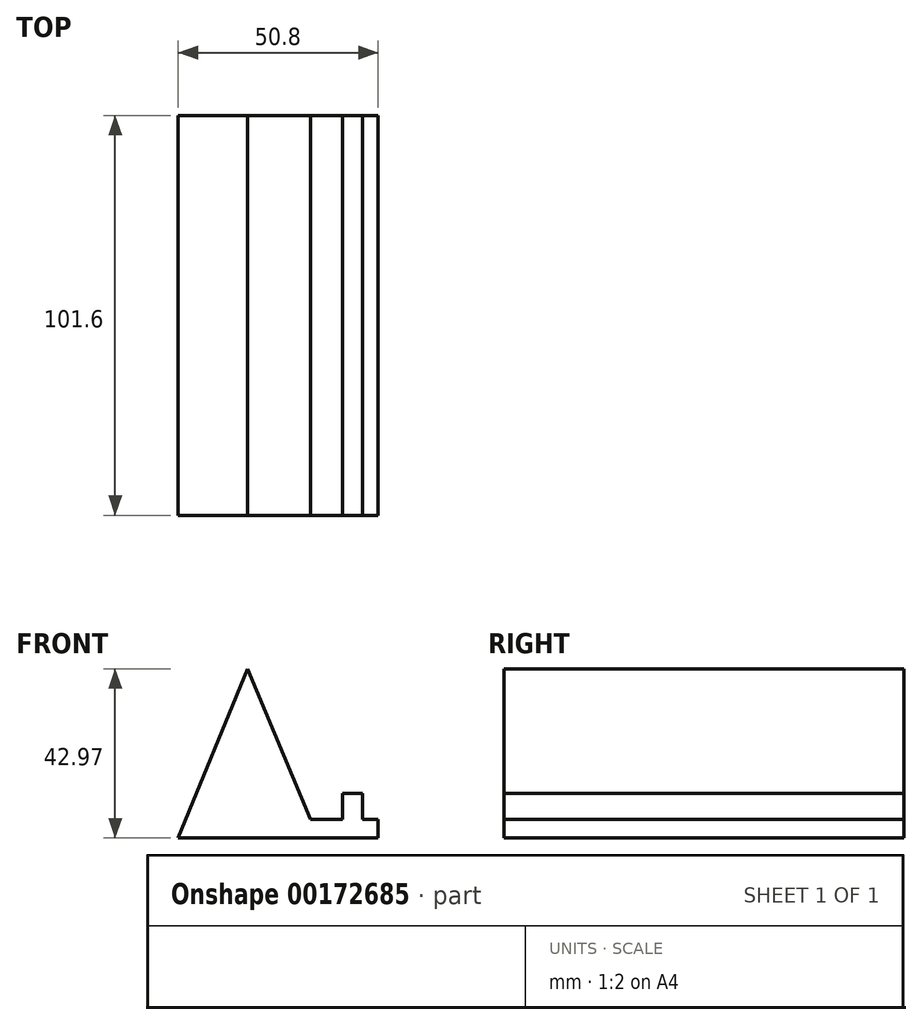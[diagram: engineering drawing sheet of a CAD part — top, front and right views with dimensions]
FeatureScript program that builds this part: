
annotation { "Feature Type Name" : "Feature", "Feature Type Description" : "" }
export const myFeature = defineFeature(function(context is Context, id is Id, definition is map)
    precondition{}
    {
        {
            var Q0;
            Q0=qCreatedBy(makeId("Front.planeOp"),FACE);
            var sketch = newSketch(context, id + "F0", { "sketchPlane" : qUnion([Q0])});
            skLineSegment(sketch, "E0", {"start": v(-75.09, 42.97) * mm, "end": v(-92.72, 0) * mm});
            skLineSegment(sketch, "E1", {"start": v(-59.1, 4.67) * mm, "end": v(-50.96, 4.67) * mm});
            skLineSegment(sketch, "E2", {"start": v(-50.96, 4.67) * mm, "end": v(-50.96, 11.3) * mm});
            skLineSegment(sketch, "E3", {"start": v(-50.96, 11.3) * mm, "end": v(-45.84, 11.3) * mm});
            skLineSegment(sketch, "E4", {"start": v(-45.84, 11.3) * mm, "end": v(-45.84, 4.67) * mm});
            skLineSegment(sketch, "E5", {"start": v(-92.72, 0) * mm, "end": v(-41.92, 0) * mm});
            skLineSegment(sketch, "E6", {"start": v(-45.84, 4.67) * mm, "end": v(-41.92, 4.67) * mm});
            skLineSegment(sketch, "E7", {"start": v(-41.92, 4.67) * mm, "end": v(-41.92, 0) * mm});
            skLineSegment(sketch, "E8", {"start": v(-59.1, 4.67) * mm, "end": v(-75.09, 42.97) * mm});
            skSolve(sketch);
        }
        {
            var Q0;
            Q0=makeQuery(id+"F0.imprint","IMPRINT",FACE,{"disambiguationData":[TD([[makeQuery(id+"F0.imprint","IMPRINT",EDGE,{"derivedFrom":sQuery(id+"F0.wireOp",EDGE,"E0")}),1.0]])]});
            extrude(context, id + "F1", {"entities" : qUnion([Q0]), "depth" : 101.6 * mm});
        }
    });
